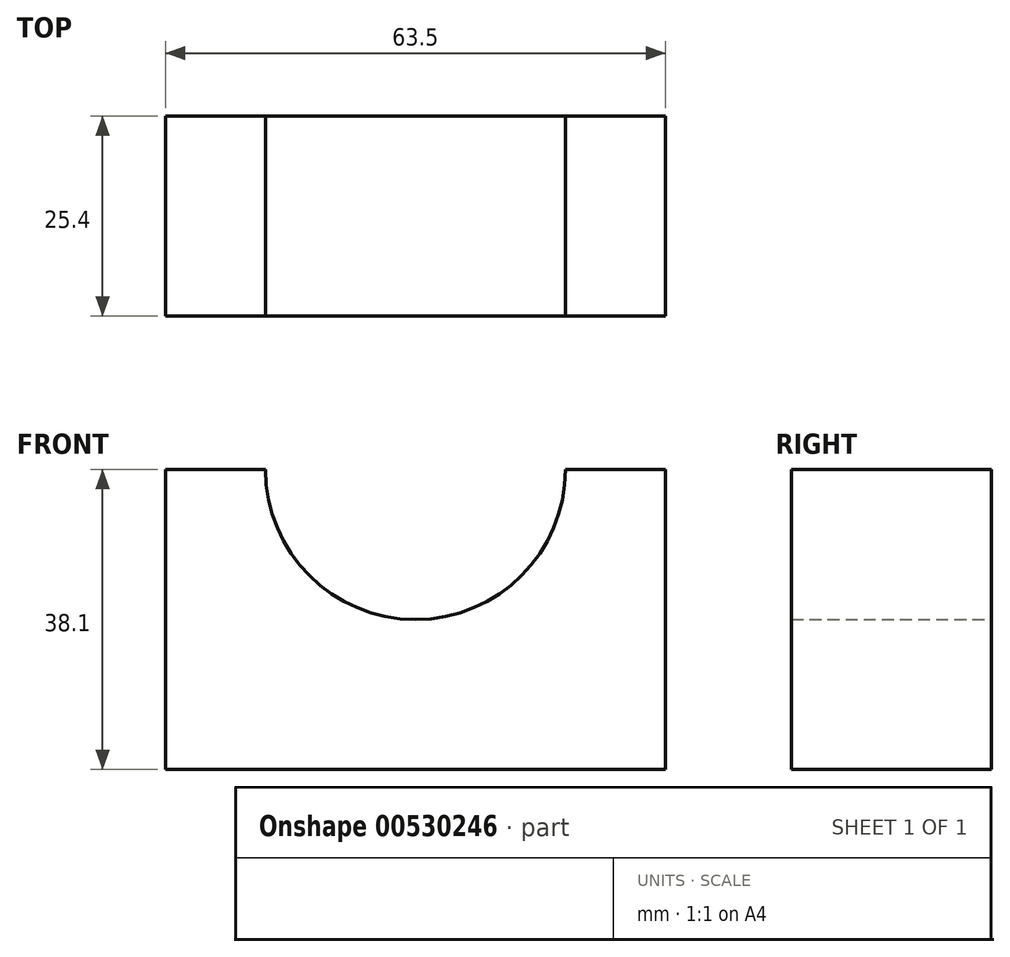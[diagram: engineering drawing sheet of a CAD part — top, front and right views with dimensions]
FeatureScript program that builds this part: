
annotation { "Feature Type Name" : "Feature", "Feature Type Description" : "" }
export const myFeature = defineFeature(function(context is Context, id is Id, definition is map)
    precondition{}
    {
        {
            var Q0;
            Q0=qCreatedBy(makeId("Front.planeOp"),FACE);
            var sketch = newSketch(context, id + "F0", { "sketchPlane" : qUnion([Q0])});
            skLineSegment(sketch, "E0", {"start": v(-111, 0) * mm, "end": v(-111, 38.1) * mm});
            skLineSegment(sketch, "E1", {"start": v(-111, 38.1) * mm, "end": v(-47.5, 38.1) * mm});
            skLineSegment(sketch, "E2", {"start": v(-47.5, 38.1) * mm, "end": v(-47.5, 0) * mm});
            skLineSegment(sketch, "E3", {"start": v(-47.5, 0) * mm, "end": v(-111, 0) * mm});
            skArc(sketch, "E4", {"start": v(-98.3, 38.1) * mm, "mid": v(-79.25, 19.05) * mm, "end": v(-60.2, 38.1) * mm});
            skSolve(sketch);
        }
        {
            var Q0;
            {var subQ3=sQuery(id+"F0.wireOp",EDGE,"E0");Q0=makeQuery(id+"F0.imprint","IMPRINT",FACE,{"disambiguationData":[TD([[makeQuery(id+"F0.imprint","IMPRINT",EDGE,{"derivedFrom":subQ3}),-1.0]])]});}
            extrude(context, id + "F1", {"entities" : qUnion([Q0]), "depth" : 25.4 * mm, "offsetDistance" : 25.4 * mm});
        }
    });
